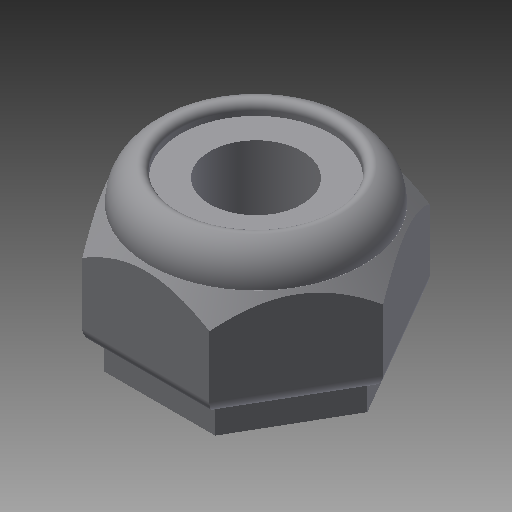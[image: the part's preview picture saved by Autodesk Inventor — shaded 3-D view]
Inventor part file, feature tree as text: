
AUTODESK INVENTOR PART (.ipt)
format: ipt  version: 2018 (Build 220112000, 112)  size: 173,056 bytes
history: native  units: in
note: dims shown in document units (in); Inventor stores cm internally (conversion verified against a paired STEP export)
features: extrude x1, other x1, imported_body x1
ambient origin geometry x8: Origin, YZ Plane, XZ Plane, XY Plane, X Axis, Y Axis, Z Axis, Center Point
bodies: Body1 (feature_tree)
feature tree (3):
  extrude  "Extrude1"  [1 undecoded]
  other  "NUT-832-NYLOCK.ipt1"
  imported_body  "Base1"
note: 1 required parameter value undecoded (feature->parameter linkage not recoverable at this tier; creation-order binding heuristic only, values carry confidence <= 0.55)
